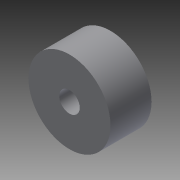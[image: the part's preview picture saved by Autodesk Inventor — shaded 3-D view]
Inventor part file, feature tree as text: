
AUTODESK INVENTOR PART (.ipt)
format: ipt  version: 2013 (Build 170138000, 138)  size: 79,360 bytes
history: native  units: in
note: dims shown in document units (in); Inventor stores cm internally (conversion verified against a paired STEP export)
features: extrude x2, sketch x2
ambient origin geometry x8: Origin, YZ Plane, XZ Plane, XY Plane, X Axis, Y Axis, Z Axis, Center Point
bodies: Solid1 (feature_tree)
feature tree (4):
  extrude  "Extrusion1"  Depth=0.375in TaperAngle=0.0deg
  extrude  "Extrusion2"  Depth=1.0in TaperAngle=0.0deg
  sketch  "Sketch1"  dims[d0=0.75in d1=0.375in d2=0.0in]
  sketch  "Sketch2"  dims[d3=0.1875in d4=1.0in d5=0.0in]
